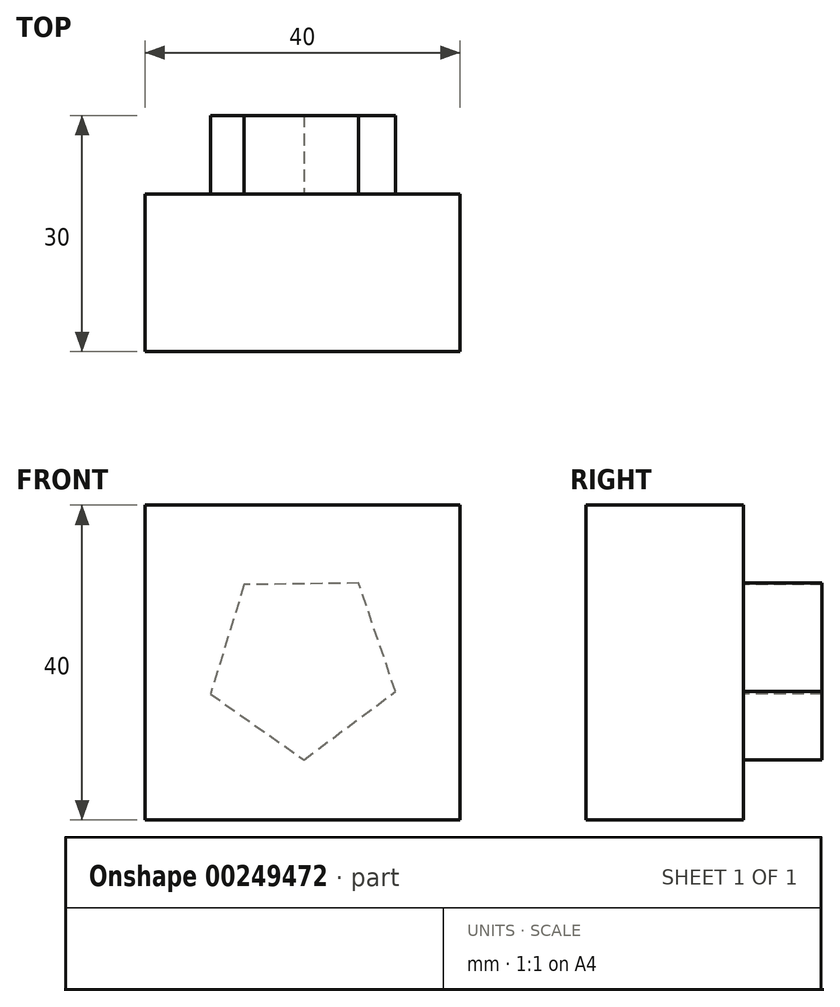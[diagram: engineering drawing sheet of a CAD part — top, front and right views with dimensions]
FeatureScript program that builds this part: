
annotation { "Feature Type Name" : "Feature", "Feature Type Description" : "" }
export const myFeature = defineFeature(function(context is Context, id is Id, definition is map)
    precondition{}
    {
        {
            var Q0;
            Q0=qCreatedBy(makeId("Front.planeOp"),FACE);
            var sketch = newSketch(context, id + "F0", { "sketchPlane" : qUnion([Q0])});
            skLineSegment(sketch, "E0.bottom", {"start": v(20, -20) * mm, "end": v(-20, -20) * mm});
            skLineSegment(sketch, "E0.top", {"start": v(20, 20) * mm, "end": v(-20, 20) * mm});
            skLineSegment(sketch, "E0.left", {"start": v(20, -20) * mm, "end": v(20, 20) * mm});
            skLineSegment(sketch, "E0.right", {"start": v(-20, -20) * mm, "end": v(-20, 20) * mm});
            skPoint(sketch, "E0.middle", {"position": v(0, 0) * mm});
            skSolve(sketch);
        }
        {
            var Q0;
            Q0=makeQuery(id+"F0.imprint","IMPRINT",FACE,{"disambiguationData":[TD([[makeQuery(id+"F0.imprint","IMPRINT",EDGE,{"derivedFrom":sQuery(id+"F0.wireOp",EDGE,"E0.bottom")}),-1.0]])]});
            extrude(context, id + "F1", {"entities" : qUnion([Q0]), "depth" : 20 * mm});
        }
        {
            var Q0;
            Q0=makeQuery(id+"F1.opExtrude","CAP_FACE",FACE,{"disambiguationData":[OSD([sQuery(id+"F0.wireOp",EDGE,"E0.bottom"),sQuery(id+"F0.wireOp",EDGE,"E0.top"),sQuery(id+"F0.wireOp",EDGE,"E0.left"),sQuery(id+"F0.wireOp",EDGE,"E0.right")])],"isStart":true});
            var sketch = newSketch(context, id + "F2", { "sketchPlane" : qUnion([Q0])});
            skCircle(sketch, "E1.cCircle", {"center": v(0, 0) * mm, "radius": 10 * mm, "construction": true});
            skLineSegment(sketch, "E1.0", {"start": v(-0.16, -12.36) * mm, "end": v(-11.8, -3.67) * mm});
            skLineSegment(sketch, "E1.1", {"start": v(-11.8, -3.67) * mm, "end": v(-7.13, 10.1) * mm});
            skLineSegment(sketch, "E1.2", {"start": v(-7.13, 10.1) * mm, "end": v(7.4, 9.9) * mm});
            skLineSegment(sketch, "E1.3", {"start": v(7.4, 9.9) * mm, "end": v(11.7, -3.97) * mm});
            skLineSegment(sketch, "E1.4", {"start": v(11.7, -3.97) * mm, "end": v(-0.16, -12.36) * mm});
            skPoint(sketch, "E1.0.midPoint", {"position": v(-5.98, -8.01) * mm});
            skSolve(sketch);
        }
        {
            var Q0;
            Q0=makeQuery(id+"F2.imprint","IMPRINT",FACE,{"disambiguationData":[TD([[makeQuery(id+"F2.imprint","IMPRINT",EDGE,{"derivedFrom":sQuery(id+"F2.wireOp",EDGE,"E1.0")}),-1.0]])]});
            extrude(context, id + "F3", {"entities" : qUnion([Q0]), "operationType" : NewBodyOperationType.ADD, "depth" : 10 * mm});
        }
    });
